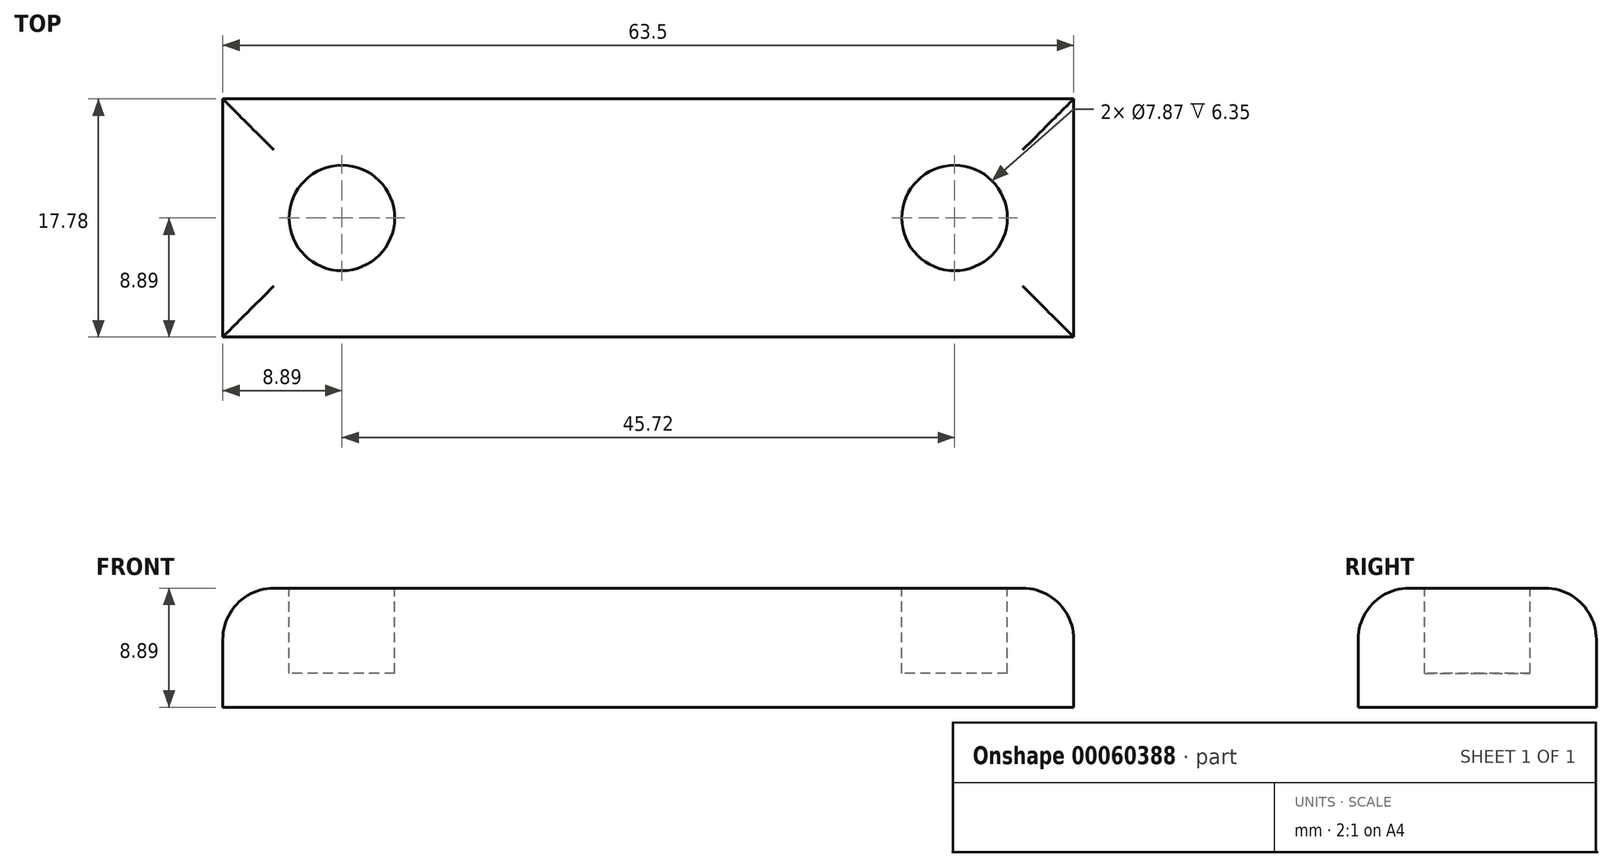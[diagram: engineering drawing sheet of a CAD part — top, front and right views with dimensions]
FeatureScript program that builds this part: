
annotation { "Feature Type Name" : "Feature", "Feature Type Description" : "" }
export const myFeature = defineFeature(function(context is Context, id is Id, definition is map)
    precondition{}
    {
        {
            var Q0;
            Q0=qCreatedBy(makeId("Top.planeOp"),FACE);
            var sketch = newSketch(context, id + "F0", { "sketchPlane" : qUnion([Q0])});
            skLineSegment(sketch, "E0.bottom", {"start": v(0, 0) * mm, "end": v(63.5, 0) * mm});
            skLineSegment(sketch, "E0.top", {"start": v(0, 17.78) * mm, "end": v(63.5, 17.78) * mm});
            skLineSegment(sketch, "E0.left", {"start": v(0, 0) * mm, "end": v(0, 17.78) * mm});
            skLineSegment(sketch, "E0.right", {"start": v(63.5, 0) * mm, "end": v(63.5, 17.78) * mm});
            skSolve(sketch);
        }
        {
            var Q0;
            Q0 = qSketchRegion(id + "F0", true);
            extrude(context, id + "F1", {"entities" : qUnion([Q0]), "depth" : 8.9 * mm});
        }
        {
            var Q0;
            Q0=makeQuery(id+"F1.opExtrude","CAP_FACE",FACE,{"disambiguationData":[OSD([sQuery(id+"F0.wireOp",EDGE,"E0.bottom"),sQuery(id+"F0.wireOp",EDGE,"E0.top"),sQuery(id+"F0.wireOp",EDGE,"E0.left"),sQuery(id+"F0.wireOp",EDGE,"E0.right")])],"isStart":false});
            var sketch = newSketch(context, id + "F2", { "sketchPlane" : qUnion([Q0])});
            skCircle(sketch, "E1", {"center": v(8.9, 8.89) * mm, "radius": 3.94 * mm});
            skCircle(sketch, "E2", {"center": v(54.61, 8.89) * mm, "radius": 3.94 * mm});
            skSolve(sketch);
        }
        {
            var Q0;
            Q0 = qSketchRegion(id + "F2", true);
            extrude(context, id + "F3", {"entities" : qUnion([Q0]), "operationType" : NewBodyOperationType.REMOVE, "oppositeDirection" : true, "depth" : 6.35 * mm});
        }
        {
            var Q0;
            Q0=makeQuery(id+"F1.opExtrude","CAP_EDGE",EDGE,{"disambiguationData":[OSD([sQuery(id+"F0.wireOp",EDGE,"E0.bottom")])],"isStart":false});
            var Q1;
            Q1=makeQuery(id+"F1.opExtrude","CAP_EDGE",EDGE,{"disambiguationData":[OSD([sQuery(id+"F0.wireOp",EDGE,"E0.left")])],"isStart":false});
            var Q2;
            Q2=makeQuery(id+"F1.opExtrude","CAP_EDGE",EDGE,{"disambiguationData":[OSD([sQuery(id+"F0.wireOp",EDGE,"E0.top")])],"isStart":false});
            var Q3;
            Q3=makeQuery(id+"F1.opExtrude","CAP_EDGE",EDGE,{"disambiguationData":[OSD([sQuery(id+"F0.wireOp",EDGE,"E0.right")])],"isStart":false});
            fillet(context, id + "F4", {"entities" : qUnion([Q0, Q1, Q2, Q3]), "radius" : 3.8 * mm, "tangentPropagation" : true, "allowEdgeOverflow" : false});
        }
    });
